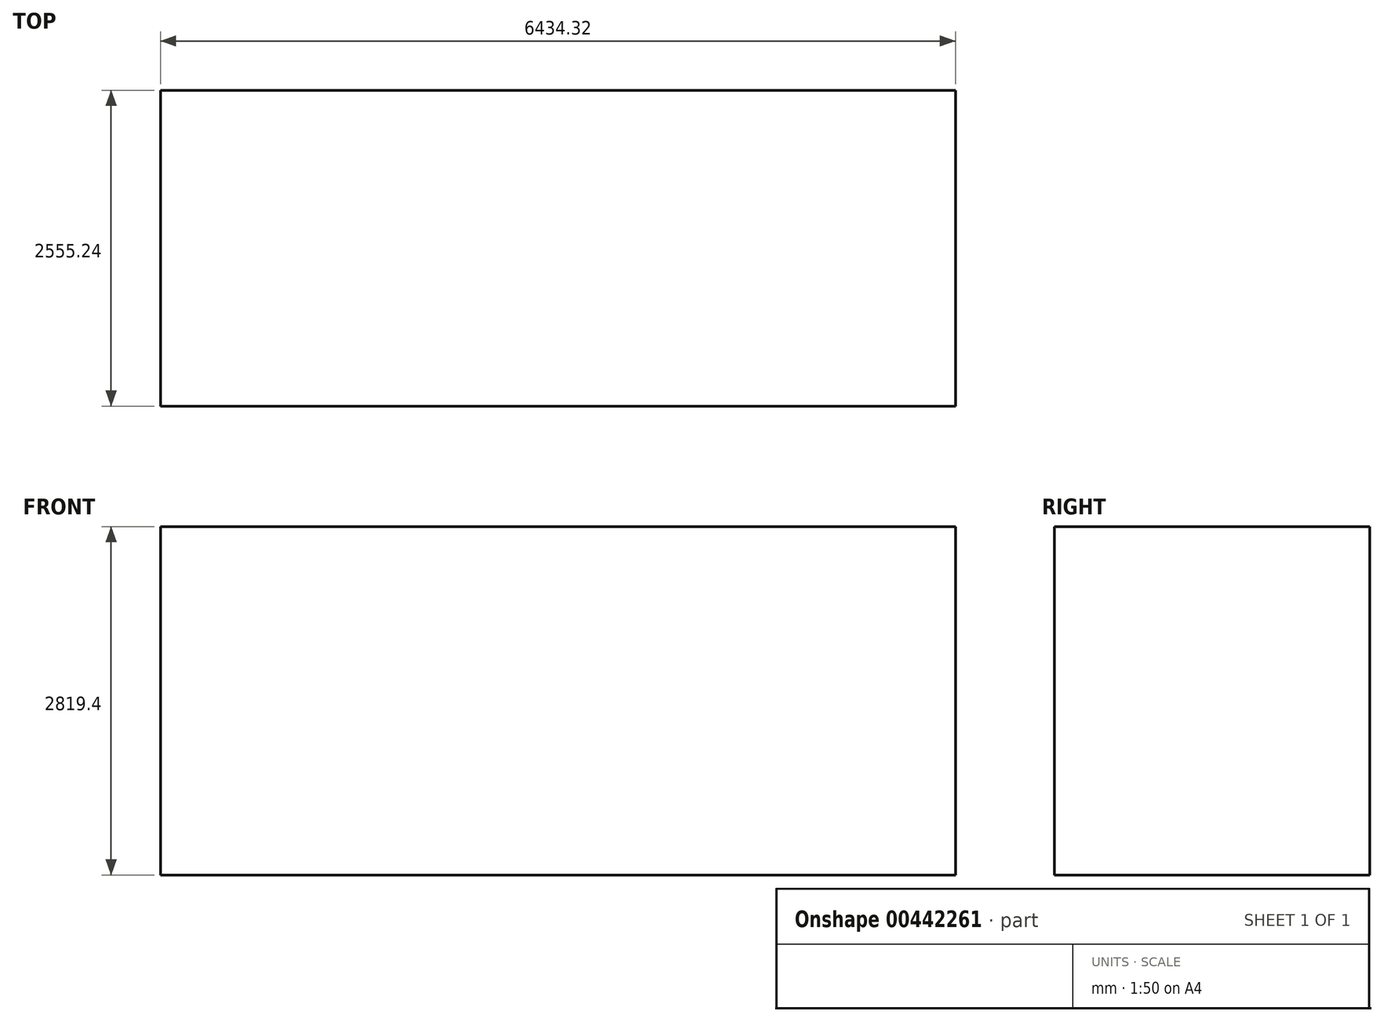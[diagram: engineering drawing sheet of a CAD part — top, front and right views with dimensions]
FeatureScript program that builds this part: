
annotation { "Feature Type Name" : "Feature", "Feature Type Description" : "" }
export const myFeature = defineFeature(function(context is Context, id is Id, definition is map)
    precondition{}
    {
        {
            var Q0;
            Q0=qCreatedBy(makeId("Front.planeOp"),FACE);
            var sketch = newSketch(context, id + "F0", { "sketchPlane" : qUnion([Q0])});
            skLineSegment(sketch, "E0.bottom", {"start": v(3214.38, -2382.67) * mm, "end": v(-3219.94, -2382.67) * mm});
            skLineSegment(sketch, "E0.top", {"start": v(3214.38, 436.73) * mm, "end": v(-3219.94, 436.73) * mm});
            skLineSegment(sketch, "E0.left", {"start": v(3214.38, -2382.67) * mm, "end": v(3214.38, 436.73) * mm});
            skLineSegment(sketch, "E0.right", {"start": v(-3219.94, -2382.67) * mm, "end": v(-3219.94, 436.73) * mm});
            skSolve(sketch);
        }
        {
            var Q0;
            Q0 = qSketchRegion(id + "F0", true);
            extrude(context, id + "F1", {"entities" : qUnion([Q0]), "depth" : 2555.24 * mm});
        }
    });
